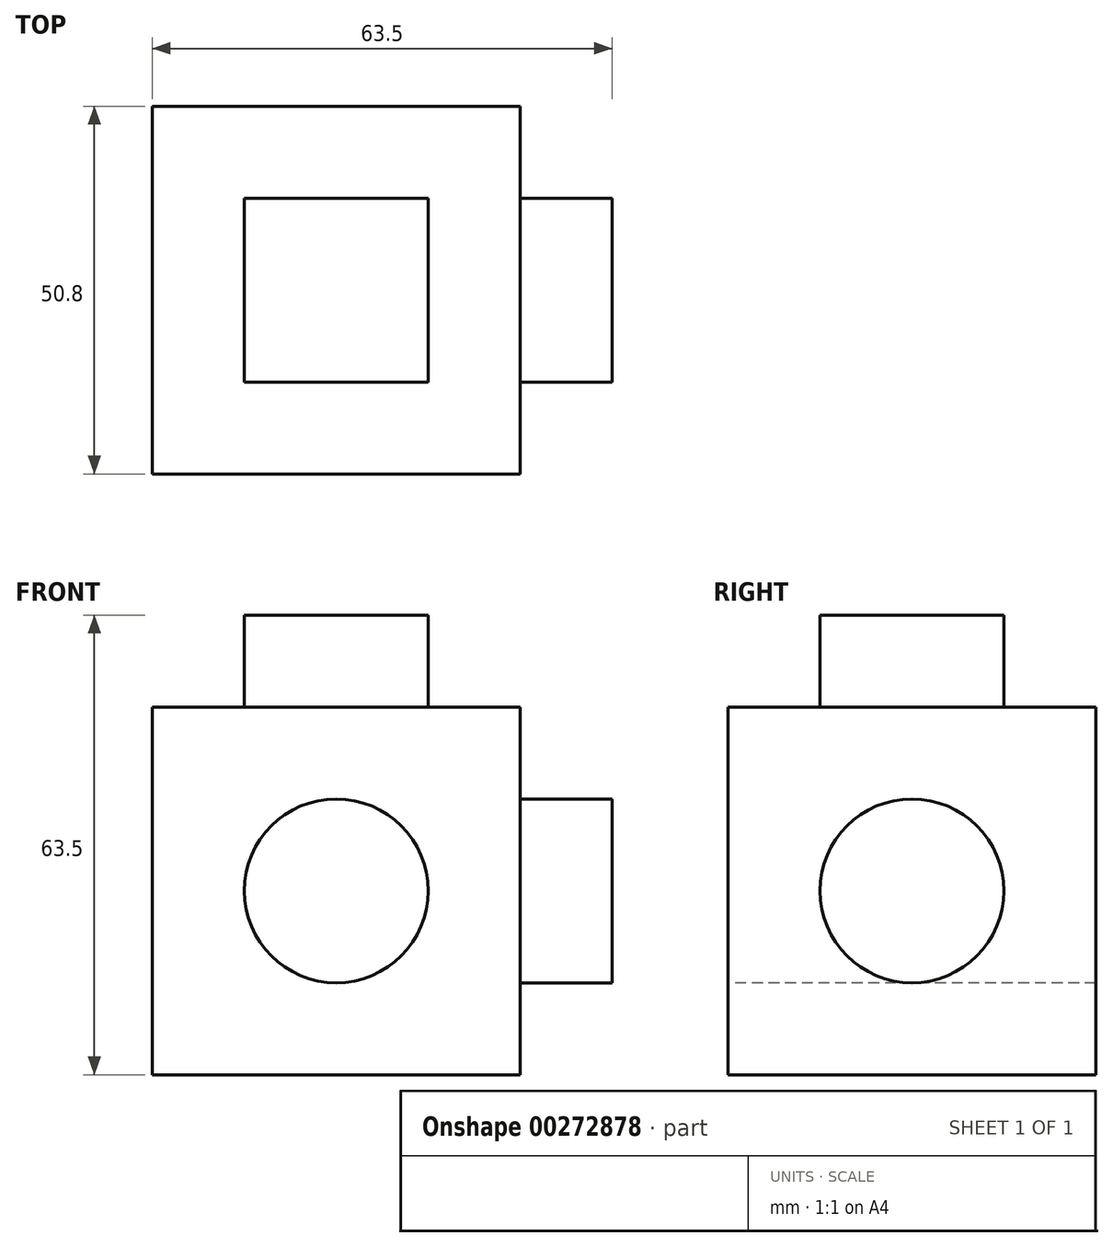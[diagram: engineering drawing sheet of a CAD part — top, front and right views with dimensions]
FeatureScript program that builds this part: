
annotation { "Feature Type Name" : "Feature", "Feature Type Description" : "" }
export const myFeature = defineFeature(function(context is Context, id is Id, definition is map)
    precondition{}
    {
        {
            var Q0;
            Q0=qCreatedBy(makeId("Front.planeOp"),FACE);
            var sketch = newSketch(context, id + "F0", { "sketchPlane" : qUnion([Q0])});
            skLineSegment(sketch, "E0.bottom", {"start": v(0, 0) * mm, "end": v(-50.8, 0) * mm});
            skLineSegment(sketch, "E0.top", {"start": v(0, 50.8) * mm, "end": v(-50.8, 50.8) * mm});
            skLineSegment(sketch, "E0.left", {"start": v(0, 0) * mm, "end": v(0, 50.8) * mm});
            skLineSegment(sketch, "E0.right", {"start": v(-50.8, 0) * mm, "end": v(-50.8, 50.8) * mm});
            skSolve(sketch);
        }
        {
            var Q0;
            Q0 = qSketchRegion(id + "F0", true);
            extrude(context, id + "F1", {"entities" : qUnion([Q0]), "depth" : 50.8 * mm});
        }
        {
            var Q0;
            Q0=makeQuery(id+"F1.opExtrude","CAP_FACE",FACE,{"disambiguationData":[OSD([sQuery(id+"F0.wireOp",EDGE,"E0.bottom"),sQuery(id+"F0.wireOp",EDGE,"E0.top"),sQuery(id+"F0.wireOp",EDGE,"E0.left"),sQuery(id+"F0.wireOp",EDGE,"E0.right")])],"isStart":false});
            var sketch = newSketch(context, id + "F2", { "sketchPlane" : qUnion([Q0])});
            skCircle(sketch, "E1", {"center": v(-25.4, 25.4) * mm, "radius": 12.7 * mm});
            skSolve(sketch);
        }
        {
            var Q0;
            Q0 = qSketchRegion(id + "F2", true);
            extrude(context, id + "F3", {"entities" : qUnion([Q0]), "operationType" : NewBodyOperationType.REMOVE, "oppositeDirection" : true, "depth" : 50.8 * mm});
        }
        {
            var Q0;
            Q0=makeQuery(id+"F1.opExtrude","SWEPT_FACE",FACE,{"disambiguationData":[OSD([sQuery(id+"F0.wireOp",EDGE,"E0.left")])]});
            var sketch = newSketch(context, id + "F4", { "sketchPlane" : qUnion([Q0])});
            skCircle(sketch, "E2", {"center": v(-25.4, 25.4) * mm, "radius": 12.7 * mm});
            skSolve(sketch);
        }
        {
            var Q0;
            Q0 = qSketchRegion(id + "F4", true);
            extrude(context, id + "F5", {"entities" : qUnion([Q0]), "operationType" : NewBodyOperationType.ADD, "depth" : 12.7 * mm});
        }
        {
            var Q0;
            Q0=makeQuery(id+"F1.opExtrude","SWEPT_FACE",FACE,{"disambiguationData":[OSD([sQuery(id+"F0.wireOp",EDGE,"E0.top")])]});
            var sketch = newSketch(context, id + "F6", { "sketchPlane" : qUnion([Q0])});
            skLineSegment(sketch, "E3.bottom", {"start": v(-38.1, -12.7) * mm, "end": v(-12.7, -12.7) * mm});
            skLineSegment(sketch, "E3.top", {"start": v(-38.1, -38.1) * mm, "end": v(-12.7, -38.1) * mm});
            skLineSegment(sketch, "E3.left", {"start": v(-38.1, -12.7) * mm, "end": v(-38.1, -38.1) * mm});
            skLineSegment(sketch, "E3.right", {"start": v(-12.7, -12.7) * mm, "end": v(-12.7, -38.1) * mm});
            skSolve(sketch);
        }
        {
            var Q0;
            Q0 = qSketchRegion(id + "F6", true);
            extrude(context, id + "F7", {"entities" : qUnion([Q0]), "operationType" : NewBodyOperationType.ADD, "depth" : 12.7 * mm});
        }
    });
